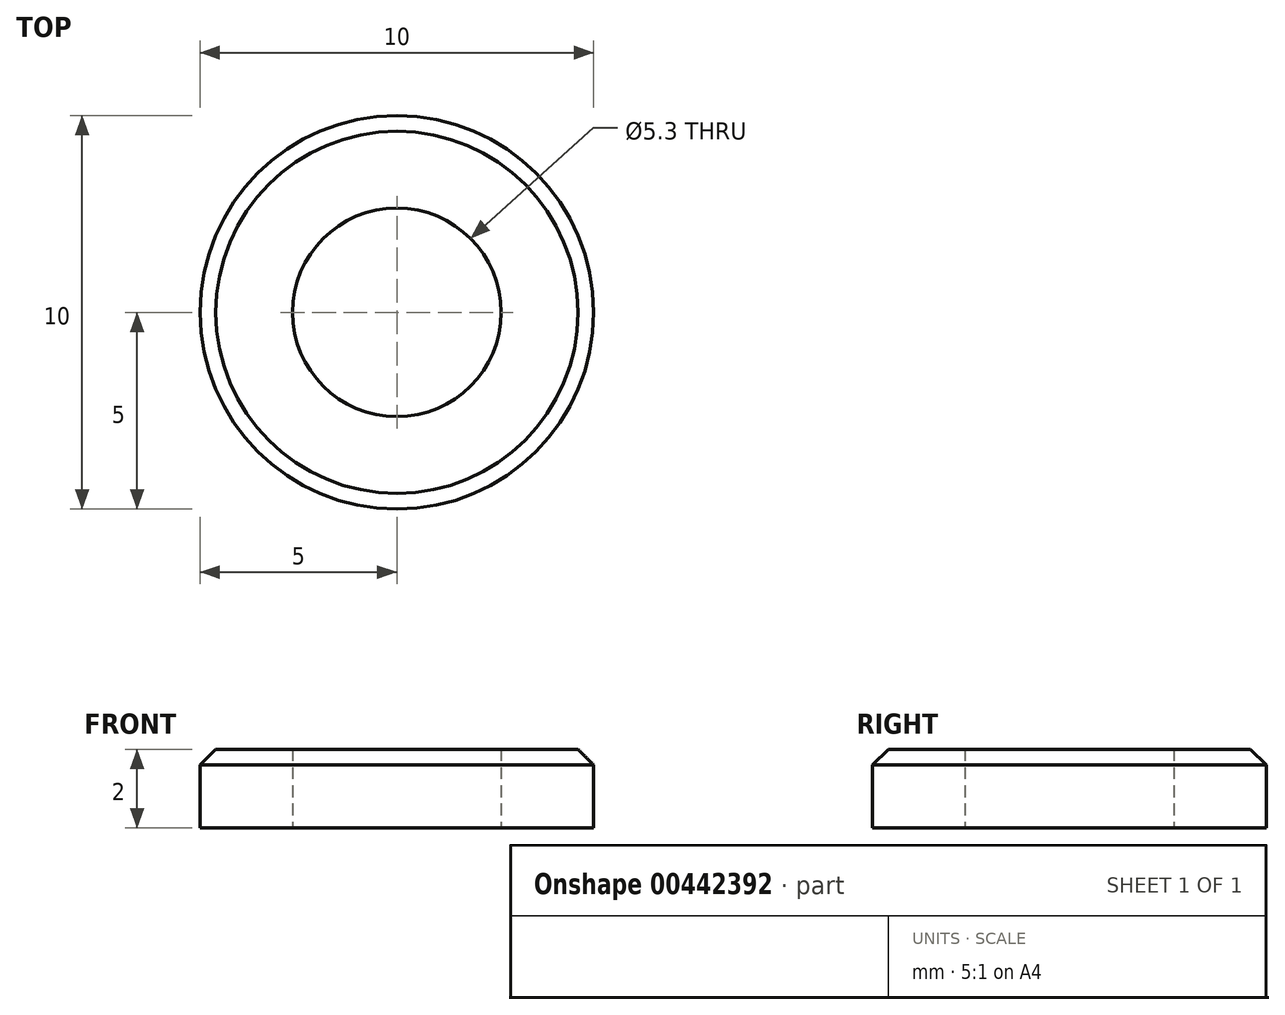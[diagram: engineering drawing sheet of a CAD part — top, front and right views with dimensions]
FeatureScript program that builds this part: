
annotation { "Feature Type Name" : "Feature", "Feature Type Description" : "" }
export const myFeature = defineFeature(function(context is Context, id is Id, definition is map)
    precondition{}
    {
        {
            var Q0;
            Q0=qCreatedBy(makeId("Top.planeOp"),FACE);
            var sketch = newSketch(context, id + "F0", { "sketchPlane" : qUnion([Q0])});
            skCircle(sketch, "E0", {"center": v(0, 0) * mm, "radius": 2.65 * mm});
            skCircle(sketch, "E1", {"center": v(0, 0) * mm, "radius": 5 * mm});
            skSolve(sketch);
        }
        {
            var Q0;
            Q0=makeQuery(id+"F0.imprint","IMPRINT",FACE,{"disambiguationData":[TD([[makeQuery(id+"F0.imprint","IMPRINT",EDGE,{"derivedFrom":sQuery(id+"F0.wireOp",EDGE,"E0")}),-1.0]])]});
            extrude(context, id + "F1", {"entities" : qUnion([Q0]), "depth" : 2 * mm, "offsetDistance" : 25 * mm});
        }
        {
            var Q0;
            Q0=makeQuery(id+"F1.opExtrude","CAP_EDGE",EDGE,{"disambiguationData":[OSD([sQuery(id+"F0.wireOp",EDGE,"E1")])],"isStart":false});
            chamfer(context, id + "F2", {"entities" : qUnion([Q0]), "width" : .4 * mm, "tangentPropagation" : true});
        }
    });
